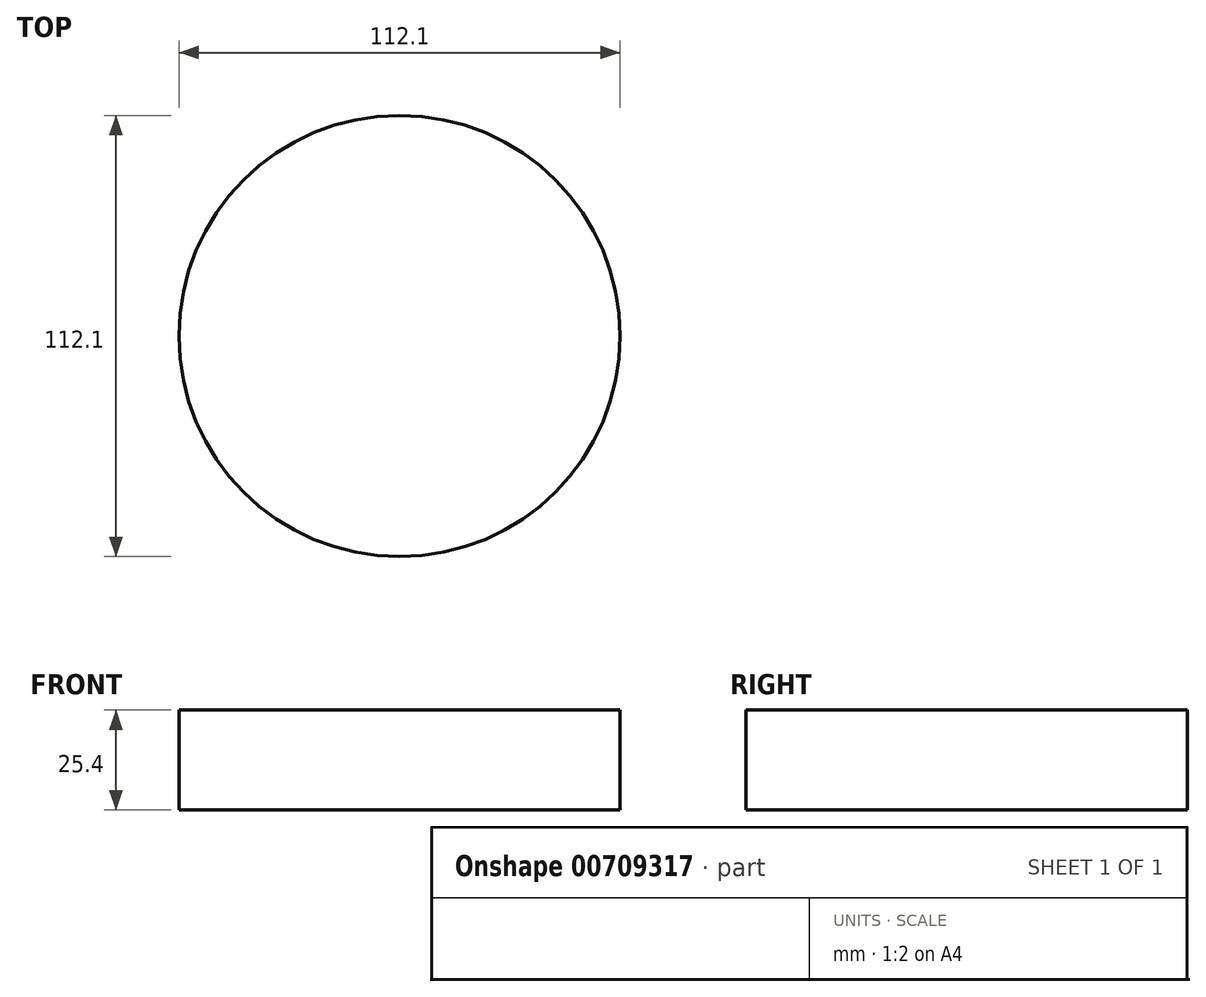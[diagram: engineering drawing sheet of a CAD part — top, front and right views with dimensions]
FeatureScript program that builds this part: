
annotation { "Feature Type Name" : "Feature", "Feature Type Description" : "" }
export const myFeature = defineFeature(function(context is Context, id is Id, definition is map)
    precondition{}
    {
        {
            var Q0;
            Q0=qCreatedBy(makeId("Top.planeOp"),FACE);
            var sketch = newSketch(context, id + "F0", { "sketchPlane" : qUnion([Q0])});
            skCircle(sketch, "E0", {"center": v(0, 0) * mm, "radius": 56.05 * mm});
            skSolve(sketch);
        }
        {
            var Q0;
            Q0=makeQuery(id+"F0.imprint","IMPRINT",FACE,{"disambiguationData":[TD([[makeQuery(id+"F0.imprint","IMPRINT",EDGE,{"derivedFrom":sQuery(id+"F0.wireOp",EDGE,"E0")}),1.0]])]});
            extrude(context, id + "F1", {"entities" : qUnion([Q0]), "depth" : 25.4 * mm, "offsetDistance" : 25.4 * mm});
        }
    });
